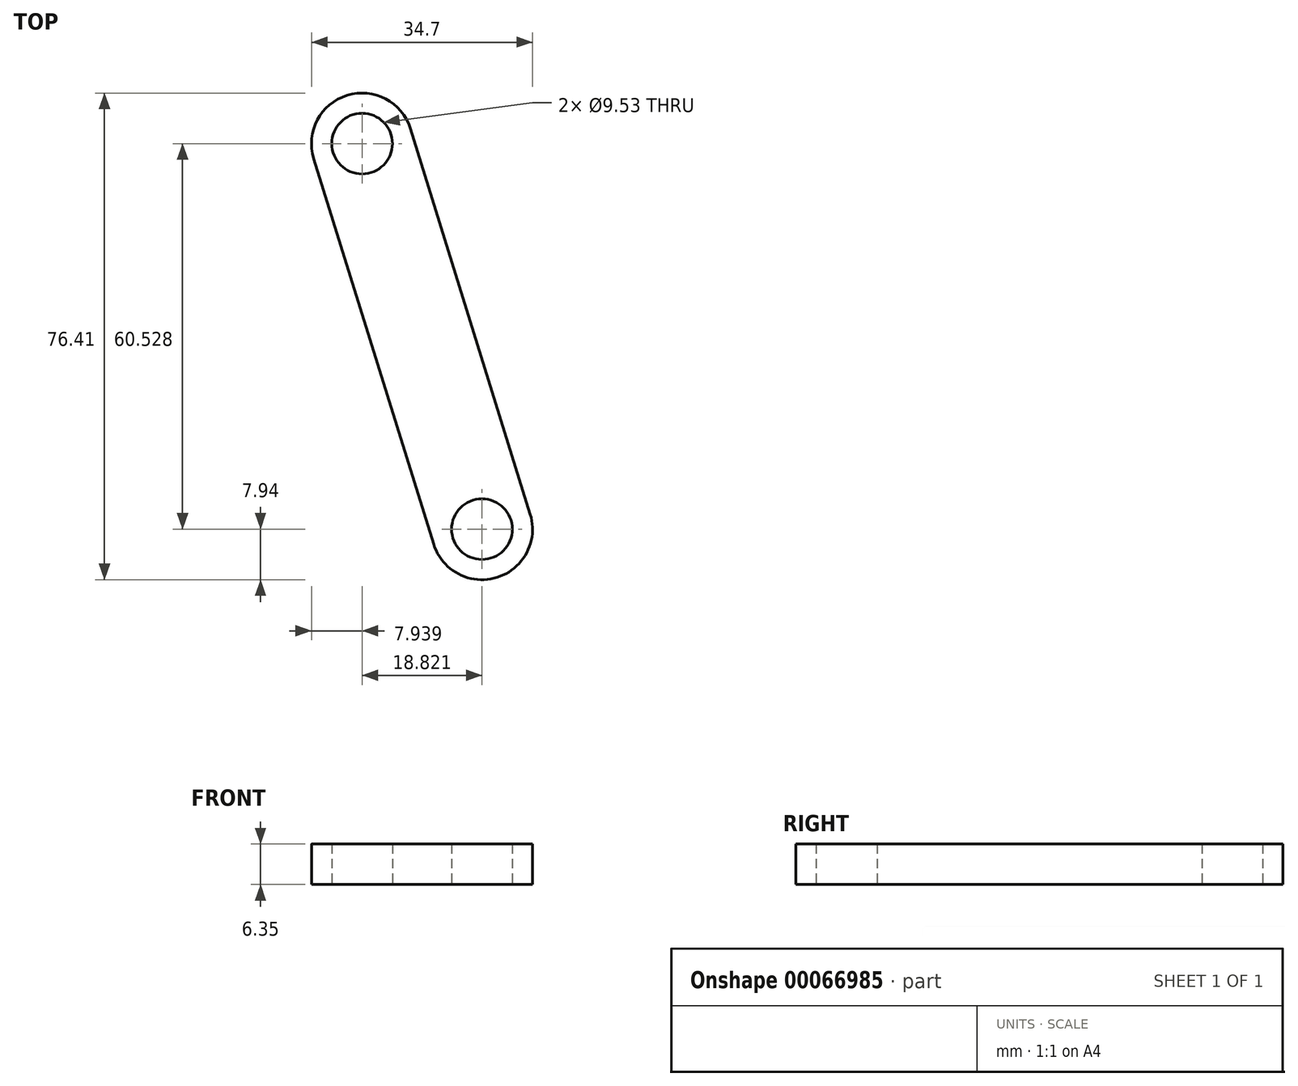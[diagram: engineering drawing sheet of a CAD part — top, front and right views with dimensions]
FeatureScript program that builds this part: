
annotation { "Feature Type Name" : "Feature", "Feature Type Description" : "" }
export const myFeature = defineFeature(function(context is Context, id is Id, definition is map)
    precondition{}
    {
        {
            var Q0;
            Q0=qCreatedBy(makeId("Top.planeOp"),FACE);
            var sketch = newSketch(context, id + "F0", { "sketchPlane" : qUnion([Q0])});
            skPoint(sketch, "E0", {"position": v(0, 0) * mm});
            skPoint(sketch, "E1", {"position": v(-18.82, 60.53) * mm});
            skArc(sketch, "E2", {"start": v(-11.24, 62.89) * mm, "mid": v(-21.18, 68.1) * mm, "end": v(-26.4, 58.17) * mm});
            skArc(sketch, "E3", {"start": v(-7.58, -2.36) * mm, "mid": v(2.36, -7.58) * mm, "end": v(7.58, 2.36) * mm});
            skLineSegment(sketch, "E4", {"start": v(-26.4, 58.17) * mm, "end": v(-7.58, -2.36) * mm});
            skLineSegment(sketch, "E5", {"start": v(7.58, 2.36) * mm, "end": v(-11.24, 62.89) * mm});
            skCircle(sketch, "E6", {"center": v(-18.82, 60.53) * mm, "radius": 4.76 * mm});
            skCircle(sketch, "E7", {"center": v(0, 0) * mm, "radius": 4.76 * mm});
            skSolve(sketch);
        }
        {
            var Q0;
            Q0=makeQuery(id+"F0.imprint","IMPRINT",FACE,{"disambiguationData":[TD([[makeQuery(id+"F0.imprint","IMPRINT",EDGE,{"derivedFrom":sQuery(id+"F0.wireOp",EDGE,"Ai0Cc8II-vgpo-Go2o-Dz2q-lxTFkMQ77an6")}),-1.0]])]});
            var Q1;
            Q1=makeQuery(id+"F0.imprint","IMPRINT",FACE,{"disambiguationData":[TD([[makeQuery(id+"F0.imprint","IMPRINT",EDGE,{"derivedFrom":sQuery(id+"F0.wireOp",EDGE,"E2")}),1.0]])]});
            extrude(context, id + "F1", {"entities" : qUnion([Q0, Q1]), "depth" : 6.35 * mm});
        }
    });
